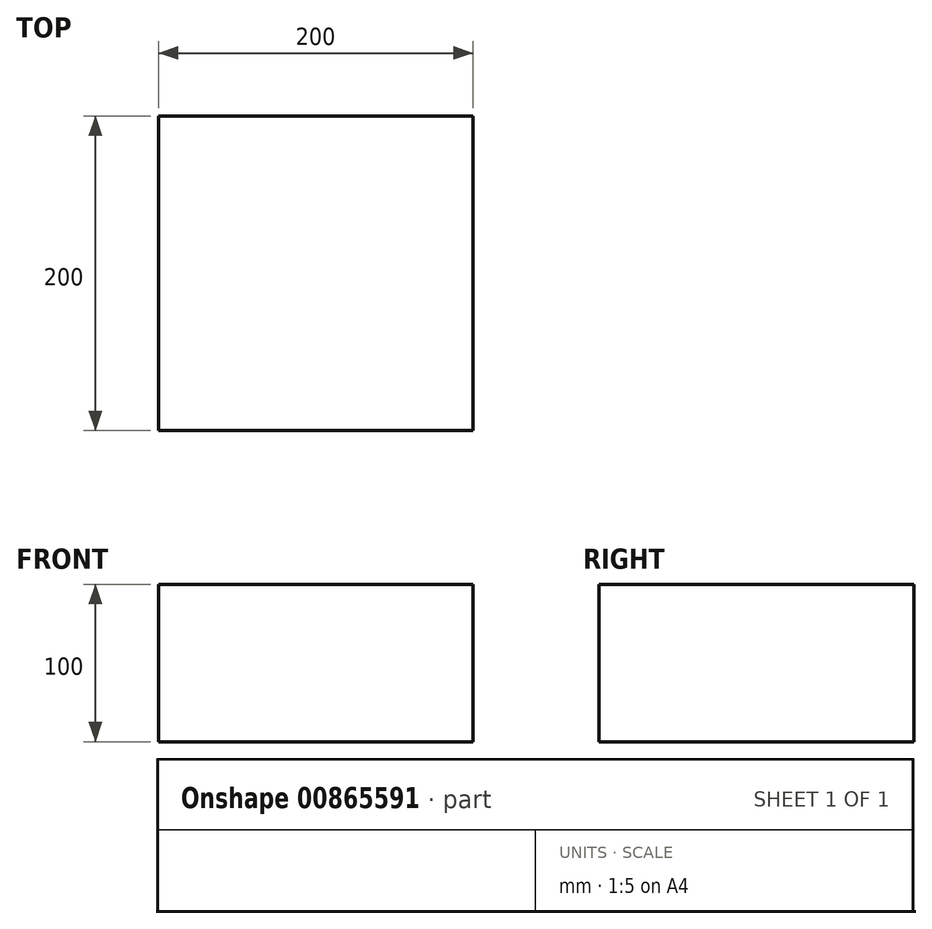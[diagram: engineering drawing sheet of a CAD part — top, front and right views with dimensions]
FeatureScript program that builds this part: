
annotation { "Feature Type Name" : "Feature", "Feature Type Description" : "" }
export const myFeature = defineFeature(function(context is Context, id is Id, definition is map)
    precondition{}
    {
        {
            assignVariable(context, id + "F0", {"name" : "c", "anyValue" : 100});
        }
        {
            var Q0;
            Q0=qCreatedBy(makeId("Top.planeOp"),FACE);
            var sketch = newSketch(context, id + "F1", { "sketchPlane" : qUnion([Q0])});
            skLineSegment(sketch, "E0.bottom", {"start": v(0, 200) * mm, "end": v(200, 200) * mm});
            skLineSegment(sketch, "E0.top", {"start": v(0, 0) * mm, "end": v(200, 0) * mm});
            skLineSegment(sketch, "E0.left", {"start": v(0, 200) * mm, "end": v(0, 0) * mm});
            skLineSegment(sketch, "E0.right", {"start": v(200, 200) * mm, "end": v(200, 0) * mm});
            skSolve(sketch);
        }
        {
            var Q0;
            Q0=makeQuery(id+"F1.imprint","IMPRINT",FACE,{"disambiguationData":[TD([[makeQuery(id+"F1.imprint","IMPRINT",EDGE,{"derivedFrom":sQuery(id+"F1.wireOp",EDGE,"E0.bottom")}),-1.0]])]});
            extrude(context, id + "F2", {"entities" : qUnion([Q0]), "depth" : (getVariable(context, 'c')) * mm, "offsetDistance" : 25 * mm});
        }
    });
